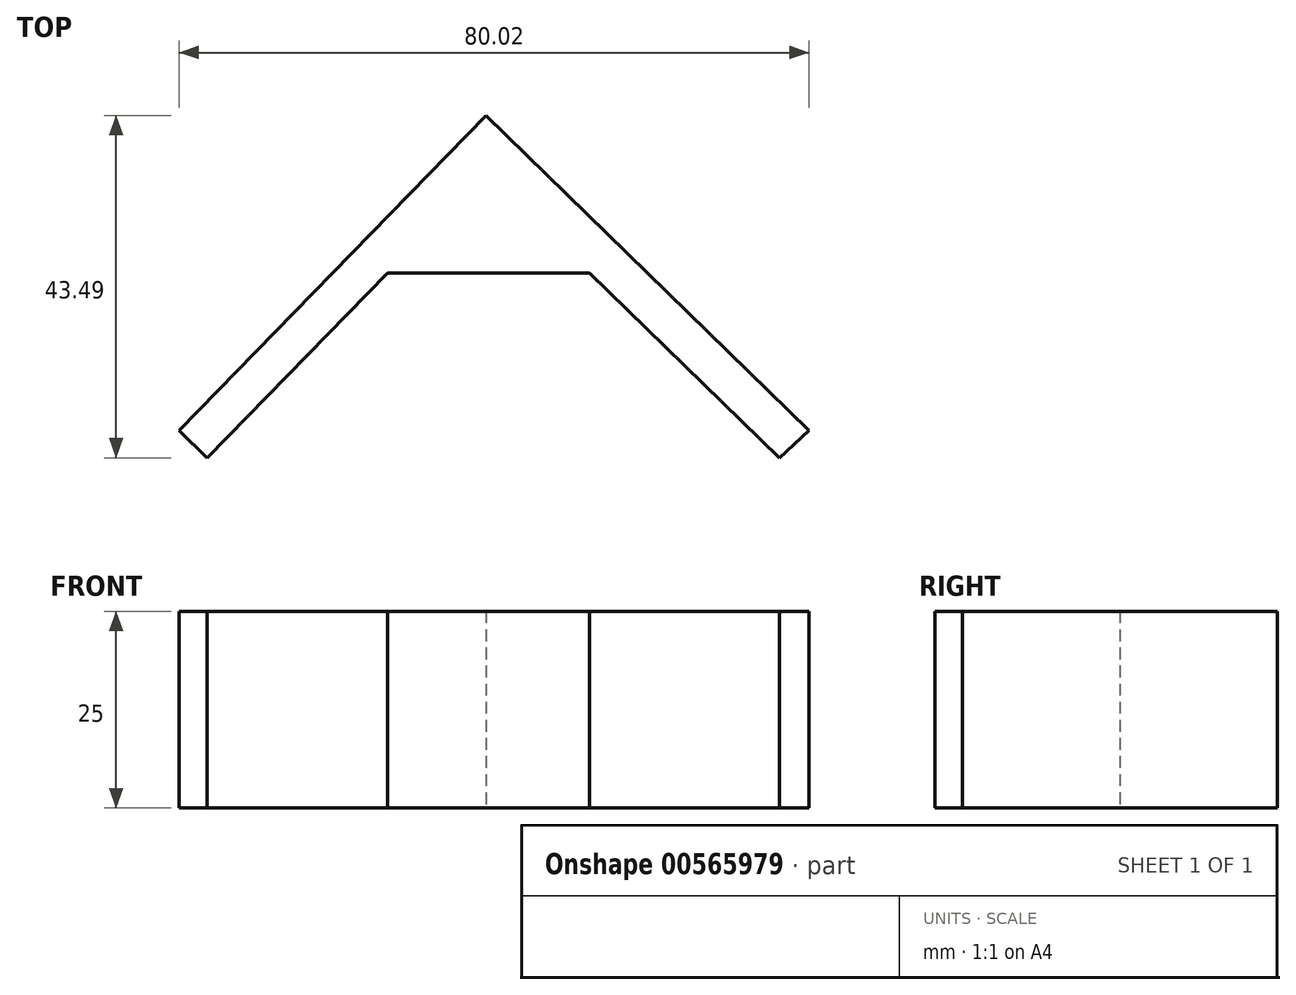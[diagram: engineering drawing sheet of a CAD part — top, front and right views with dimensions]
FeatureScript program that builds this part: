
annotation { "Feature Type Name" : "Feature", "Feature Type Description" : "" }
export const myFeature = defineFeature(function(context is Context, id is Id, definition is map)
    precondition{}
    {
        {
            var Q0;
            Q0=qCreatedBy(makeId("Top.planeOp"),FACE);
            var sketch = newSketch(context, id + "F0", { "sketchPlane" : qUnion([Q0])});
            skPoint(sketch, "E0", {"position": v(0, 40) * mm});
            skPoint(sketch, "E1", {"position": v(-39, 0) * mm});
            skPoint(sketch, "E2", {"position": v(41.03, 0) * mm});
            skLineSegment(sketch, "E3", {"start": v(-39, 0) * mm, "end": v(0, 40) * mm});
            skLineSegment(sketch, "E4", {"start": v(41.03, 0) * mm, "end": v(0, 40) * mm});
            skLineSegment(sketch, "E5", {"start": v(-39, 0) * mm, "end": v(-35.41, -3.5) * mm});
            skLineSegment(sketch, "E6", {"start": v(-35.41, -3.5) * mm, "end": v(0, 32.84) * mm});
            skLineSegment(sketch, "E7", {"start": v(0, 32.84) * mm, "end": v(37.27, -3.5) * mm});
            skLineSegment(sketch, "E8", {"start": v(37.27, -3.5) * mm, "end": v(41.03, 0) * mm});
            skLineSegment(sketch, "E9", {"start": v(-12.51, 20) * mm, "end": v(13.17, 20) * mm});
            skSolve(sketch);
        }
        {
            var Q0;
            Q0=makeQuery(id+"F0.imprint","IMPRINT",FACE,{"disambiguationData":[TD([[makeQuery(id+"F0.imprint","IMPRINT",EDGE,{"derivedFrom":sQuery(id+"F0.wireOp",EDGE,"E3")}),-1.0]])]});
            var Q1;
            {var subQ3=sQuery(id+"F0.wireOp",EDGE,"E9");Q1=makeQuery(id+"F0.imprint","IMPRINT",FACE,{"disambiguationData":[TD([[makeQuery(id+"F0.imprint","IMPRINT",EDGE,{"derivedFrom":subQ3}),1.0]])]});}
            extrude(context, id + "F1", {"entities" : qUnion([Q0, Q1]), "depth" : 25 * mm, "offsetDistance" : 25 * mm});
        }
    });
